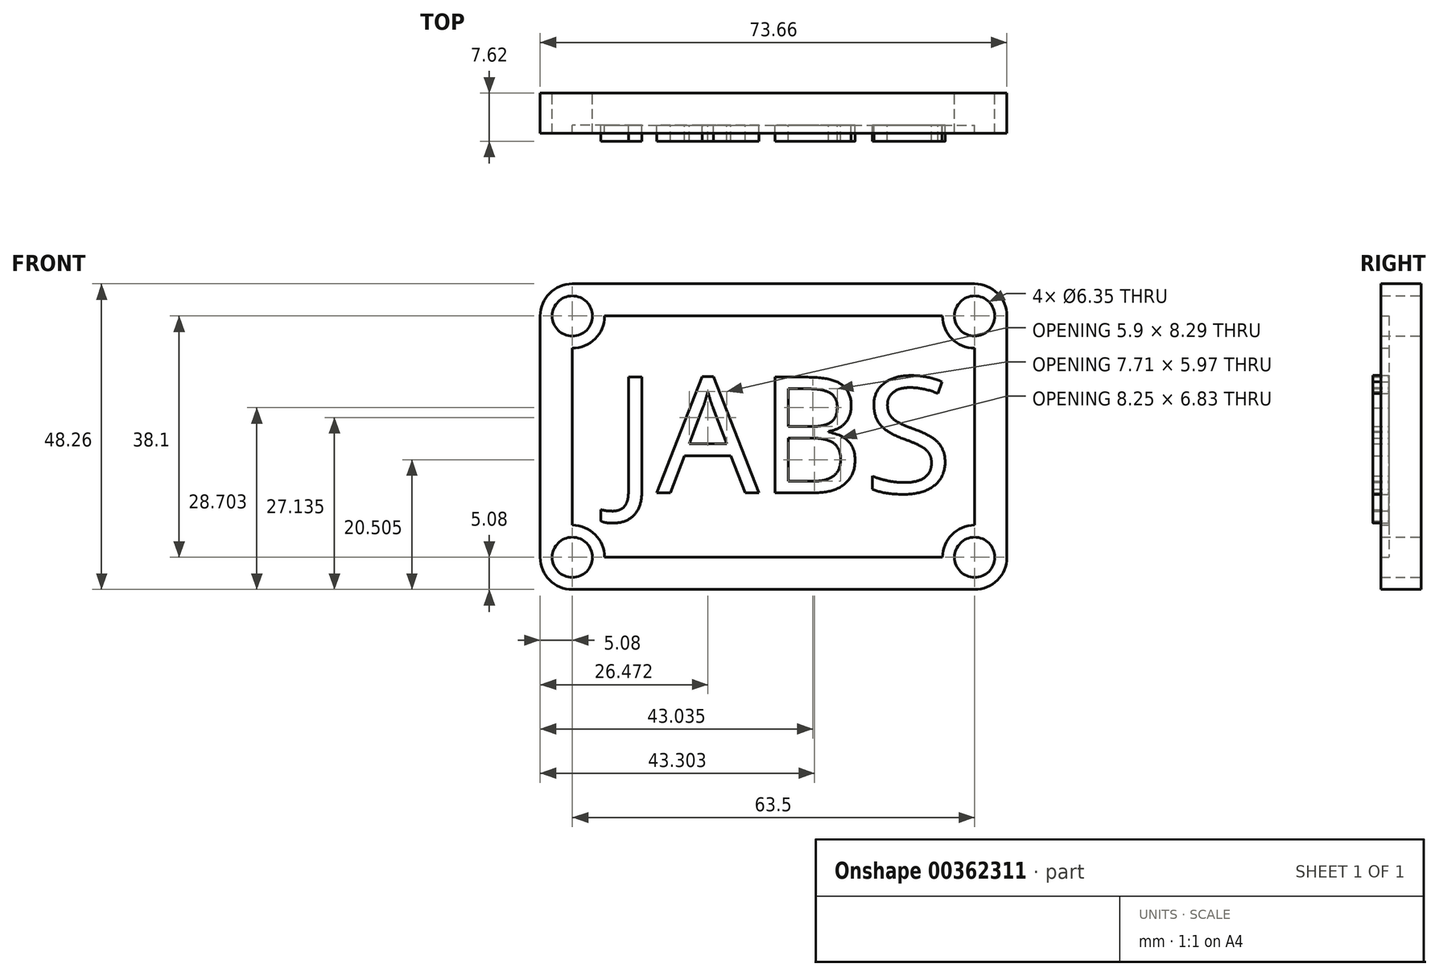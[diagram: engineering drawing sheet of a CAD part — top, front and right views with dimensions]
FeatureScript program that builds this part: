
annotation { "Feature Type Name" : "Feature", "Feature Type Description" : "" }
export const myFeature = defineFeature(function(context is Context, id is Id, definition is map)
    precondition{}
    {
        {
            var Q0;
            Q0=qCreatedBy(makeId("Front.planeOp"),FACE);
            var sketch = newSketch(context, id + "F0", { "sketchPlane" : qUnion([Q0])});
            skLineSegment(sketch, "E0.bottom", {"start": v(0, 0) * mm, "end": v(63.5, 0) * mm});
            skLineSegment(sketch, "E0.top", {"start": v(0, -38.1) * mm, "end": v(63.5, -38.1) * mm});
            skLineSegment(sketch, "E0.left", {"start": v(0, 0) * mm, "end": v(0, -38.1) * mm});
            skLineSegment(sketch, "E0.right", {"start": v(63.5, 0) * mm, "end": v(63.5, -38.1) * mm});
            skLineSegment(sketch, "E1.0", {"start": v(0, 5.08) * mm, "end": v(63.5, 5.08) * mm});
            skLineSegment(sketch, "E1.1", {"start": v(-5.08, 0) * mm, "end": v(-5.08, -38.1) * mm});
            skLineSegment(sketch, "E1.2", {"start": v(0, -43.18) * mm, "end": v(63.5, -43.18) * mm});
            skLineSegment(sketch, "E1.3", {"start": v(68.58, 0) * mm, "end": v(68.58, -38.1) * mm});
            skCircle(sketch, "E2", {"center": v(63.5, 0) * mm, "radius": 3.18 * mm});
            skCircle(sketch, "E3", {"center": v(0, 0) * mm, "radius": 3.18 * mm});
            skCircle(sketch, "E4", {"center": v(63.5, -38.1) * mm, "radius": 3.18 * mm});
            skCircle(sketch, "E5", {"center": v(0, -38.1) * mm, "radius": 3.18 * mm});
            skPoint(sketch, "E6.visualSharp", {"position": v(68.58, 5.08) * mm});
            skPoint(sketch, "E7.visualSharp", {"position": v(-5.08, 5.08) * mm});
            skPoint(sketch, "E8.visualSharp", {"position": v(-5.08, -43.18) * mm});
            skPoint(sketch, "E9.visualSharp", {"position": v(68.58, -43.18) * mm});
            skCircle(sketch, "E10", {"center": v(63.5, 0) * mm, "radius": 5.08 * mm});
            skCircle(sketch, "E11", {"center": v(63.5, -38.1) * mm, "radius": 5.08 * mm});
            skCircle(sketch, "E12", {"center": v(0, -38.1) * mm, "radius": 5.08 * mm});
            skCircle(sketch, "E13", {"center": v(0, 0) * mm, "radius": 5.08 * mm});
            skSolve(sketch);
        }
        {
            var Q0;
            {var subQ5=sQuery(id+"F0.wireOp",EDGE,"E1.3");Q0=makeQuery(id+"F0.imprint","IMPRINT",FACE,{"disambiguationData":[TD([[makeQuery(id+"F0.imprint","IMPRINT",EDGE,{"derivedFrom":subQ5}),-1.0]])]});}
            var Q1;
            {var subQ5=sQuery(id+"F0.wireOp",EDGE,"E1.0");Q1=makeQuery(id+"F0.imprint","IMPRINT",FACE,{"disambiguationData":[TD([[makeQuery(id+"F0.imprint","IMPRINT",EDGE,{"derivedFrom":subQ5}),-1.0]])]});}
            var Q2;
            {var subQ5=sQuery(id+"F0.wireOp",EDGE,"E1.1");Q2=makeQuery(id+"F0.imprint","IMPRINT",FACE,{"disambiguationData":[TD([[makeQuery(id+"F0.imprint","IMPRINT",EDGE,{"derivedFrom":subQ5}),1.0]])]});}
            var Q3;
            {var subQ5=sQuery(id+"F0.wireOp",EDGE,"E1.2");Q3=makeQuery(id+"F0.imprint","IMPRINT",FACE,{"disambiguationData":[TD([[makeQuery(id+"F0.imprint","IMPRINT",EDGE,{"derivedFrom":subQ5}),1.0]])]});}
            var Q4;
            {var subQ0=sQuery(id+"F0.wireOp",EDGE,"E10");var subQ4=sQuery(id+"F0.wireOp",EDGE,"E0.bottom");var subQ8=makeQuery(id+"F0.imprint","INTERSECT",VERTEX,{"derivedFrom":[subQ4,subQ0]});Q4=makeQuery(id+"F0.imprint","IMPRINT",FACE,{"disambiguationData":[TD([[makeQuery(id+"F0.imprint","IMPRINT",EDGE,{"disambiguationData":[TD([[subQ8,-1.0]])],"derivedFrom":subQ4}),1.0]])]});}
            var Q5;
            {var subQ0=sQuery(id+"F0.wireOp",EDGE,"E10");var subQ1=sQuery(id+"F0.wireOp",EDGE,"E0.bottom");var subQ2=makeQuery(id+"F0.imprint","INTERSECT",VERTEX,{"derivedFrom":[subQ1,subQ0]});Q5=makeQuery(id+"F0.imprint","IMPRINT",FACE,{"disambiguationData":[TD([[makeQuery(id+"F0.imprint","IMPRINT",EDGE,{"disambiguationData":[TD([[subQ2,-1.0]])],"derivedFrom":subQ1}),-1.0]])]});}
            var Q6;
            {var subQ0=sQuery(id+"F0.wireOp",EDGE,"E11");var subQ5=sQuery(id+"F0.wireOp",EDGE,"E0.top");var subQ8=makeQuery(id+"F0.imprint","INTERSECT",VERTEX,{"derivedFrom":[subQ5,subQ0]});Q6=makeQuery(id+"F0.imprint","IMPRINT",FACE,{"disambiguationData":[TD([[makeQuery(id+"F0.imprint","IMPRINT",EDGE,{"disambiguationData":[TD([[subQ8,-1.0]])],"derivedFrom":subQ5}),-1.0]])]});}
            var Q7;
            {var subQ0=sQuery(id+"F0.wireOp",EDGE,"E11");var subQ1=sQuery(id+"F0.wireOp",EDGE,"E0.top");var subQ2=makeQuery(id+"F0.imprint","INTERSECT",VERTEX,{"derivedFrom":[subQ1,subQ0]});Q7=makeQuery(id+"F0.imprint","IMPRINT",FACE,{"disambiguationData":[TD([[makeQuery(id+"F0.imprint","IMPRINT",EDGE,{"disambiguationData":[TD([[subQ2,-1.0]])],"derivedFrom":subQ1}),1.0]])]});}
            var Q8;
            {var subQ3=sQuery(id+"F0.wireOp",EDGE,"E5");var subQ6=sQuery(id+"F0.wireOp",EDGE,"E0.top");var subQ7=makeQuery(id+"F0.imprint","INTERSECT",VERTEX,{"derivedFrom":[subQ6,subQ3]});Q8=makeQuery(id+"F0.imprint","IMPRINT",FACE,{"disambiguationData":[TD([[makeQuery(id+"F0.imprint","IMPRINT",EDGE,{"disambiguationData":[TD([[subQ7,-1.0]])],"derivedFrom":subQ6}),-1.0]])]});}
            var Q9;
            {var subQ0=sQuery(id+"F0.wireOp",EDGE,"E5");var subQ1=sQuery(id+"F0.wireOp",EDGE,"E0.top");var subQ2=makeQuery(id+"F0.imprint","INTERSECT",VERTEX,{"derivedFrom":[subQ1,subQ0]});Q9=makeQuery(id+"F0.imprint","IMPRINT",FACE,{"disambiguationData":[TD([[makeQuery(id+"F0.imprint","IMPRINT",EDGE,{"disambiguationData":[TD([[subQ2,-1.0]])],"derivedFrom":subQ1}),1.0]])]});}
            var Q10;
            {var subQ0=sQuery(id+"F0.wireOp",EDGE,"E3");var subQ1=sQuery(id+"F0.wireOp",EDGE,"E0.bottom");var subQ2=makeQuery(id+"F0.imprint","INTERSECT",VERTEX,{"derivedFrom":[subQ1,subQ0]});Q10=makeQuery(id+"F0.imprint","IMPRINT",FACE,{"disambiguationData":[TD([[makeQuery(id+"F0.imprint","IMPRINT",EDGE,{"disambiguationData":[TD([[subQ2,-1.0]])],"derivedFrom":subQ1}),-1.0]])]});}
            var Q11;
            {var subQ2=sQuery(id+"F0.wireOp",EDGE,"E0.bottom");var subQ4=sQuery(id+"F0.wireOp",EDGE,"E3");var subQ8=makeQuery(id+"F0.imprint","INTERSECT",VERTEX,{"derivedFrom":[subQ2,subQ4]});Q11=makeQuery(id+"F0.imprint","IMPRINT",FACE,{"disambiguationData":[TD([[makeQuery(id+"F0.imprint","IMPRINT",EDGE,{"disambiguationData":[TD([[subQ8,-1.0]])],"derivedFrom":subQ2}),1.0]])]});}
            extrude(context, id + "F1", {"entities" : qUnion([Q0, Q1, Q2, Q3, Q4, Q5, Q6, Q7, Q8, Q9, Q10, Q11]), "depth" : 6.35 * mm});
        }
        {
            var Q0;
            {var subQ5=sQuery(id+"F0.wireOp",EDGE,"E13");var subQ10=sQuery(id+"F0.wireOp",EDGE,"E0.bottom");var subQ15=makeQuery(id+"F0.imprint","INTERSECT",VERTEX,{"derivedFrom":[subQ10,subQ5]});Q0=makeQuery(id+"F0.imprint","IMPRINT",FACE,{"disambiguationData":[TD([[makeQuery(id+"F0.imprint","IMPRINT",EDGE,{"disambiguationData":[TD([[subQ15,-1.0]])],"derivedFrom":subQ10}),-1.0]])]});}
            extrude(context, id + "F2", {"entities" : qUnion([Q0]), "operationType" : NewBodyOperationType.ADD, "depth" : 5.08 * mm});
        }
        {
            var Q0;
            {var subQ0=sQuery(id+"F0.wireOp",EDGE,"E0.left");var subQ1=sQuery(id+"F0.wireOp",EDGE,"E0.bottom");var subQ2=makeQuery(id+"F0.imprint","INTERSECT",VERTEX,{"derivedFrom":[subQ1,subQ0]});Q0=makeQuery(id+"F0.imprint","IMPRINT",FACE,{"disambiguationData":[TD([[makeQuery(id+"F0.imprint","IMPRINT",EDGE,{"disambiguationData":[TD([[subQ2,-1.0]])],"derivedFrom":subQ1}),-1.0]])]});}
            extrude(context, id + "F3", {"entities" : qUnion([Q0]), "operationType" : NewBodyOperationType.REMOVE, "oppositeDirection" : true, "depth" : 25.4 * mm});
        }
        {
            var Q0;
            Q0=makeQuery(id+"F2.opExtrude","CAP_FACE",FACE,{"disambiguationData":[OSD([sQuery(id+"F0.wireOp",EDGE,"E0.bottom"),sQuery(id+"F0.wireOp",EDGE,"E0.top"),sQuery(id+"F0.wireOp",EDGE,"E0.left"),sQuery(id+"F0.wireOp",EDGE,"E0.right"),sQuery(id+"F0.wireOp",EDGE,"E10"),sQuery(id+"F0.wireOp",EDGE,"E11"),sQuery(id+"F0.wireOp",EDGE,"E12"),sQuery(id+"F0.wireOp",EDGE,"E13")])],"isStart":false});
            var sketch = newSketch(context, id + "F4", { "sketchPlane" : qUnion([Q0])});
            skText(sketch, "E14", { "text": "JABS", "fontName": "OpenSans-Regular.ttf"});
            const initialGuessF4  = {"E14": [0.01003, -0.0312, 1, 0, 0.0184]};
            skSetInitialGuess(sketch, initialGuessF4);
            skSolve(sketch);
        }
        {
            var Q0;
            Q0 = qSketchRegion(id + "F4", true);
            extrude(context, id + "F5", {"entities" : qUnion([Q0]), "depth" : 2.54 * mm});
        }
        {
            var Q0;
            Q0=makeQuery(id+"F5.opExtrude","SWEPT_BODY",BODY,{"disambiguationData":[OSD([sQuery(id+"F4.wireOp",EDGE,"E14.sketch_text.stroke-23"),sQuery(id+"F4.wireOp",EDGE,"E14.sketch_text.stroke-24"),sQuery(id+"F4.wireOp",EDGE,"E14.sketch_text.stroke-25"),sQuery(id+"F4.wireOp",EDGE,"E14.sketch_text.stroke-26"),sQuery(id+"F4.wireOp",EDGE,"E14.sketch_text.stroke-27"),sQuery(id+"F4.wireOp",EDGE,"E14.sketch_text.stroke-28"),sQuery(id+"F4.wireOp",EDGE,"E14.sketch_text.stroke-29"),sQuery(id+"F4.wireOp",EDGE,"E14.sketch_text.stroke-30"),sQuery(id+"F4.wireOp",EDGE,"E14.sketch_text.stroke-31"),sQuery(id+"F4.wireOp",EDGE,"E14.sketch_text.stroke-32"),sQuery(id+"F4.wireOp",EDGE,"E14.sketch_text.stroke-33"),sQuery(id+"F4.wireOp",EDGE,"E14.sketch_text.stroke-34"),sQuery(id+"F4.wireOp",EDGE,"E14.sketch_text.stroke-35"),sQuery(id+"F4.wireOp",EDGE,"E14.sketch_text.stroke-36"),sQuery(id+"F4.wireOp",EDGE,"E14.sketch_text.stroke-37"),sQuery(id+"F4.wireOp",EDGE,"E14.sketch_text.stroke-38"),sQuery(id+"F4.wireOp",EDGE,"E14.sketch_text.stroke-39"),sQuery(id+"F4.wireOp",EDGE,"E14.sketch_text.stroke-40"),sQuery(id+"F4.wireOp",EDGE,"E14.sketch_text.stroke-41"),sQuery(id+"F4.wireOp",EDGE,"E14.sketch_text.stroke-42"),sQuery(id+"F4.wireOp",EDGE,"E14.sketch_text.stroke-43"),sQuery(id+"F4.wireOp",EDGE,"E14.sketch_text.stroke-44"),sQuery(id+"F4.wireOp",EDGE,"E14.sketch_text.stroke-45"),sQuery(id+"F4.wireOp",EDGE,"E14.sketch_text.stroke-46"),sQuery(id+"F4.wireOp",EDGE,"E14.sketch_text.stroke-47")])]});
            var Q1;
            Q1=makeQuery(id+"F5.opExtrude","SWEPT_BODY",BODY,{"disambiguationData":[OSD([sQuery(id+"F4.wireOp",EDGE,"E14.sketch_text.stroke-10"),sQuery(id+"F4.wireOp",EDGE,"E14.sketch_text.stroke-11"),sQuery(id+"F4.wireOp",EDGE,"E14.sketch_text.stroke-12"),sQuery(id+"F4.wireOp",EDGE,"E14.sketch_text.stroke-13"),sQuery(id+"F4.wireOp",EDGE,"E14.sketch_text.stroke-14"),sQuery(id+"F4.wireOp",EDGE,"E14.sketch_text.stroke-15"),sQuery(id+"F4.wireOp",EDGE,"E14.sketch_text.stroke-16"),sQuery(id+"F4.wireOp",EDGE,"E14.sketch_text.stroke-17"),sQuery(id+"F4.wireOp",EDGE,"E14.sketch_text.stroke-18"),sQuery(id+"F4.wireOp",EDGE,"E14.sketch_text.stroke-19"),sQuery(id+"F4.wireOp",EDGE,"E14.sketch_text.stroke-20"),sQuery(id+"F4.wireOp",EDGE,"E14.sketch_text.stroke-21"),sQuery(id+"F4.wireOp",EDGE,"E14.sketch_text.stroke-22")])]});
            var Q2;
            Q2=makeQuery(id+"F5.opExtrude","SWEPT_BODY",BODY,{"disambiguationData":[OSD([sQuery(id+"F4.wireOp",EDGE,"E14.sketch_text.stroke-0"),sQuery(id+"F4.wireOp",EDGE,"E14.sketch_text.stroke-1"),sQuery(id+"F4.wireOp",EDGE,"E14.sketch_text.stroke-2"),sQuery(id+"F4.wireOp",EDGE,"E14.sketch_text.stroke-3"),sQuery(id+"F4.wireOp",EDGE,"E14.sketch_text.stroke-4"),sQuery(id+"F4.wireOp",EDGE,"E14.sketch_text.stroke-5"),sQuery(id+"F4.wireOp",EDGE,"E14.sketch_text.stroke-6"),sQuery(id+"F4.wireOp",EDGE,"E14.sketch_text.stroke-7"),sQuery(id+"F4.wireOp",EDGE,"E14.sketch_text.stroke-8"),sQuery(id+"F4.wireOp",EDGE,"E14.sketch_text.stroke-9")])]});
            var Q3;
            Q3=makeQuery(id+"F5.opExtrude","SWEPT_BODY",BODY,{"disambiguationData":[OSD([sQuery(id+"F4.wireOp",EDGE,"E14.sketch_text.stroke-48"),sQuery(id+"F4.wireOp",EDGE,"E14.sketch_text.stroke-49"),sQuery(id+"F4.wireOp",EDGE,"E14.sketch_text.stroke-50"),sQuery(id+"F4.wireOp",EDGE,"E14.sketch_text.stroke-51"),sQuery(id+"F4.wireOp",EDGE,"E14.sketch_text.stroke-52"),sQuery(id+"F4.wireOp",EDGE,"E14.sketch_text.stroke-53"),sQuery(id+"F4.wireOp",EDGE,"E14.sketch_text.stroke-54"),sQuery(id+"F4.wireOp",EDGE,"E14.sketch_text.stroke-55"),sQuery(id+"F4.wireOp",EDGE,"E14.sketch_text.stroke-56"),sQuery(id+"F4.wireOp",EDGE,"E14.sketch_text.stroke-57"),sQuery(id+"F4.wireOp",EDGE,"E14.sketch_text.stroke-58"),sQuery(id+"F4.wireOp",EDGE,"E14.sketch_text.stroke-59"),sQuery(id+"F4.wireOp",EDGE,"E14.sketch_text.stroke-60"),sQuery(id+"F4.wireOp",EDGE,"E14.sketch_text.stroke-61"),sQuery(id+"F4.wireOp",EDGE,"E14.sketch_text.stroke-62"),sQuery(id+"F4.wireOp",EDGE,"E14.sketch_text.stroke-63"),sQuery(id+"F4.wireOp",EDGE,"E14.sketch_text.stroke-64"),sQuery(id+"F4.wireOp",EDGE,"E14.sketch_text.stroke-65"),sQuery(id+"F4.wireOp",EDGE,"E14.sketch_text.stroke-66"),sQuery(id+"F4.wireOp",EDGE,"E14.sketch_text.stroke-67"),sQuery(id+"F4.wireOp",EDGE,"E14.sketch_text.stroke-68"),sQuery(id+"F4.wireOp",EDGE,"E14.sketch_text.stroke-69"),sQuery(id+"F4.wireOp",EDGE,"E14.sketch_text.stroke-70"),sQuery(id+"F4.wireOp",EDGE,"E14.sketch_text.stroke-71"),sQuery(id+"F4.wireOp",EDGE,"E14.sketch_text.stroke-72")])]});
            transform(context, id + "F6", {"entities" : qUnion([Q0, Q1, Q2, Q3]), "transformType" : TransformType.TRANSLATION_3D, "dx" : -5.08 * mm, "dy" : 0 * mm, "dz" : 3.3 * mm, "makeCopy" : false});
        }
        {
            var Q0;
            Q0=makeQuery(id+"F5.opExtrude","SWEPT_BODY",BODY,{"disambiguationData":[OSD([sQuery(id+"F4.wireOp",EDGE,"E14.sketch_text.stroke-48"),sQuery(id+"F4.wireOp",EDGE,"E14.sketch_text.stroke-49"),sQuery(id+"F4.wireOp",EDGE,"E14.sketch_text.stroke-50"),sQuery(id+"F4.wireOp",EDGE,"E14.sketch_text.stroke-51"),sQuery(id+"F4.wireOp",EDGE,"E14.sketch_text.stroke-52"),sQuery(id+"F4.wireOp",EDGE,"E14.sketch_text.stroke-53"),sQuery(id+"F4.wireOp",EDGE,"E14.sketch_text.stroke-54"),sQuery(id+"F4.wireOp",EDGE,"E14.sketch_text.stroke-55"),sQuery(id+"F4.wireOp",EDGE,"E14.sketch_text.stroke-56"),sQuery(id+"F4.wireOp",EDGE,"E14.sketch_text.stroke-57"),sQuery(id+"F4.wireOp",EDGE,"E14.sketch_text.stroke-58"),sQuery(id+"F4.wireOp",EDGE,"E14.sketch_text.stroke-59"),sQuery(id+"F4.wireOp",EDGE,"E14.sketch_text.stroke-60"),sQuery(id+"F4.wireOp",EDGE,"E14.sketch_text.stroke-61"),sQuery(id+"F4.wireOp",EDGE,"E14.sketch_text.stroke-62"),sQuery(id+"F4.wireOp",EDGE,"E14.sketch_text.stroke-63"),sQuery(id+"F4.wireOp",EDGE,"E14.sketch_text.stroke-64"),sQuery(id+"F4.wireOp",EDGE,"E14.sketch_text.stroke-65"),sQuery(id+"F4.wireOp",EDGE,"E14.sketch_text.stroke-66"),sQuery(id+"F4.wireOp",EDGE,"E14.sketch_text.stroke-67"),sQuery(id+"F4.wireOp",EDGE,"E14.sketch_text.stroke-68"),sQuery(id+"F4.wireOp",EDGE,"E14.sketch_text.stroke-69"),sQuery(id+"F4.wireOp",EDGE,"E14.sketch_text.stroke-70"),sQuery(id+"F4.wireOp",EDGE,"E14.sketch_text.stroke-71"),sQuery(id+"F4.wireOp",EDGE,"E14.sketch_text.stroke-72")])]});
            var Q1;
            Q1=makeQuery(id+"F5.opExtrude","SWEPT_BODY",BODY,{"disambiguationData":[OSD([sQuery(id+"F4.wireOp",EDGE,"E14.sketch_text.stroke-23"),sQuery(id+"F4.wireOp",EDGE,"E14.sketch_text.stroke-24"),sQuery(id+"F4.wireOp",EDGE,"E14.sketch_text.stroke-25"),sQuery(id+"F4.wireOp",EDGE,"E14.sketch_text.stroke-26"),sQuery(id+"F4.wireOp",EDGE,"E14.sketch_text.stroke-27"),sQuery(id+"F4.wireOp",EDGE,"E14.sketch_text.stroke-28"),sQuery(id+"F4.wireOp",EDGE,"E14.sketch_text.stroke-29"),sQuery(id+"F4.wireOp",EDGE,"E14.sketch_text.stroke-30"),sQuery(id+"F4.wireOp",EDGE,"E14.sketch_text.stroke-31"),sQuery(id+"F4.wireOp",EDGE,"E14.sketch_text.stroke-32"),sQuery(id+"F4.wireOp",EDGE,"E14.sketch_text.stroke-33"),sQuery(id+"F4.wireOp",EDGE,"E14.sketch_text.stroke-34"),sQuery(id+"F4.wireOp",EDGE,"E14.sketch_text.stroke-35"),sQuery(id+"F4.wireOp",EDGE,"E14.sketch_text.stroke-36"),sQuery(id+"F4.wireOp",EDGE,"E14.sketch_text.stroke-37"),sQuery(id+"F4.wireOp",EDGE,"E14.sketch_text.stroke-38"),sQuery(id+"F4.wireOp",EDGE,"E14.sketch_text.stroke-39"),sQuery(id+"F4.wireOp",EDGE,"E14.sketch_text.stroke-40"),sQuery(id+"F4.wireOp",EDGE,"E14.sketch_text.stroke-41"),sQuery(id+"F4.wireOp",EDGE,"E14.sketch_text.stroke-42"),sQuery(id+"F4.wireOp",EDGE,"E14.sketch_text.stroke-43"),sQuery(id+"F4.wireOp",EDGE,"E14.sketch_text.stroke-44"),sQuery(id+"F4.wireOp",EDGE,"E14.sketch_text.stroke-45"),sQuery(id+"F4.wireOp",EDGE,"E14.sketch_text.stroke-46"),sQuery(id+"F4.wireOp",EDGE,"E14.sketch_text.stroke-47")])]});
            var Q2;
            Q2=makeQuery(id+"F5.opExtrude","SWEPT_BODY",BODY,{"disambiguationData":[OSD([sQuery(id+"F4.wireOp",EDGE,"E14.sketch_text.stroke-10"),sQuery(id+"F4.wireOp",EDGE,"E14.sketch_text.stroke-11"),sQuery(id+"F4.wireOp",EDGE,"E14.sketch_text.stroke-12"),sQuery(id+"F4.wireOp",EDGE,"E14.sketch_text.stroke-13"),sQuery(id+"F4.wireOp",EDGE,"E14.sketch_text.stroke-14"),sQuery(id+"F4.wireOp",EDGE,"E14.sketch_text.stroke-15"),sQuery(id+"F4.wireOp",EDGE,"E14.sketch_text.stroke-16"),sQuery(id+"F4.wireOp",EDGE,"E14.sketch_text.stroke-17"),sQuery(id+"F4.wireOp",EDGE,"E14.sketch_text.stroke-18"),sQuery(id+"F4.wireOp",EDGE,"E14.sketch_text.stroke-19"),sQuery(id+"F4.wireOp",EDGE,"E14.sketch_text.stroke-20"),sQuery(id+"F4.wireOp",EDGE,"E14.sketch_text.stroke-21"),sQuery(id+"F4.wireOp",EDGE,"E14.sketch_text.stroke-22")])]});
            var Q3;
            Q3=makeQuery(id+"F5.opExtrude","SWEPT_BODY",BODY,{"disambiguationData":[OSD([sQuery(id+"F4.wireOp",EDGE,"E14.sketch_text.stroke-0"),sQuery(id+"F4.wireOp",EDGE,"E14.sketch_text.stroke-1"),sQuery(id+"F4.wireOp",EDGE,"E14.sketch_text.stroke-2"),sQuery(id+"F4.wireOp",EDGE,"E14.sketch_text.stroke-3"),sQuery(id+"F4.wireOp",EDGE,"E14.sketch_text.stroke-4"),sQuery(id+"F4.wireOp",EDGE,"E14.sketch_text.stroke-5"),sQuery(id+"F4.wireOp",EDGE,"E14.sketch_text.stroke-6"),sQuery(id+"F4.wireOp",EDGE,"E14.sketch_text.stroke-7"),sQuery(id+"F4.wireOp",EDGE,"E14.sketch_text.stroke-8"),sQuery(id+"F4.wireOp",EDGE,"E14.sketch_text.stroke-9")])]});
            transform(context, id + "F7", {"entities" : qUnion([Q0, Q1, Q2, Q3]), "transformType" : TransformType.TRANSLATION_3D, "dx" : 1.52 * mm, "dy" : 0 * mm, "dz" : 0 * mm, "makeCopy" : false});
        }
    });
